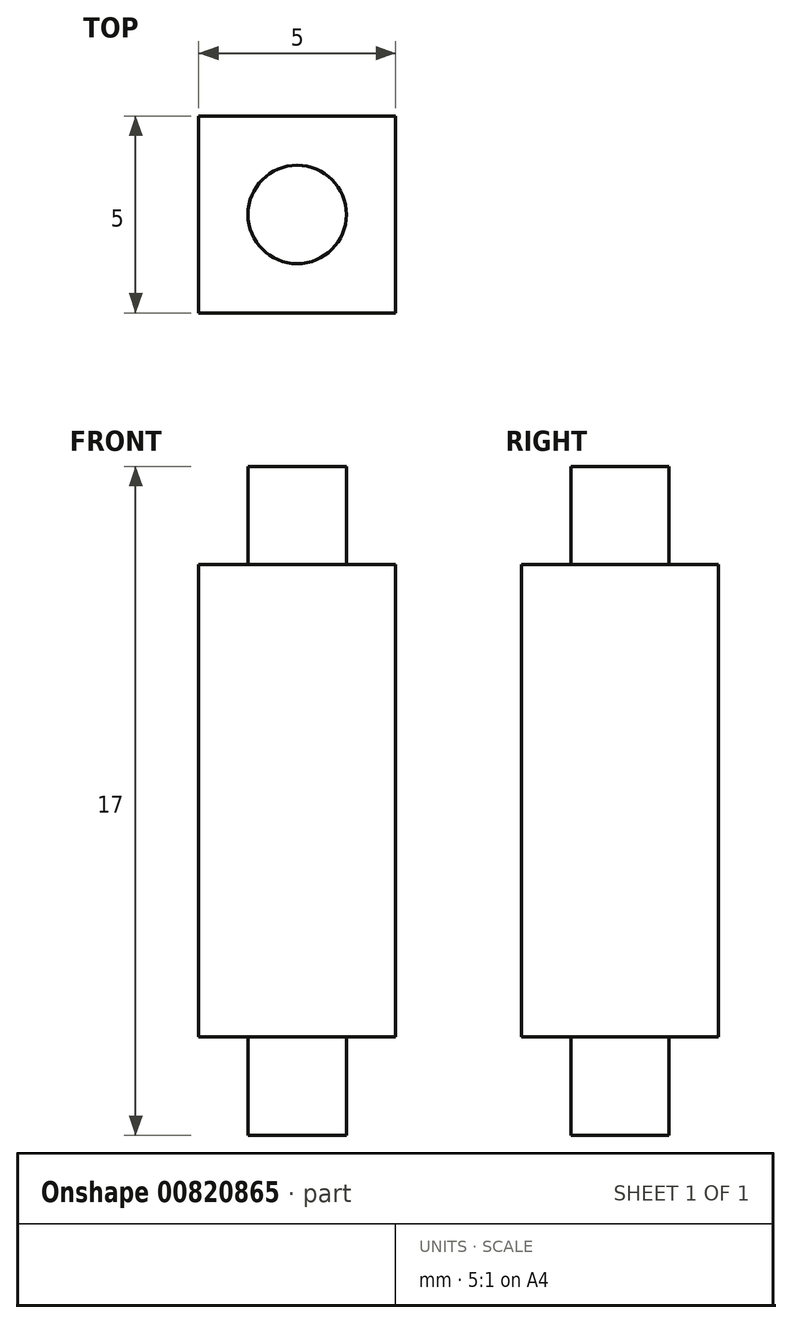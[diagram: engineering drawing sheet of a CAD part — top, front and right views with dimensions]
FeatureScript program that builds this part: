
annotation { "Feature Type Name" : "Feature", "Feature Type Description" : "" }
export const myFeature = defineFeature(function(context is Context, id is Id, definition is map)
    precondition{}
    {
        {
            var Q0;
            Q0=qCreatedBy(makeId("Top.planeOp"),FACE);
            var sketch = newSketch(context, id + "F0", { "sketchPlane" : qUnion([Q0])});
            skLineSegment(sketch, "E0.bottom", {"start": v(2.5, -2.5) * mm, "end": v(-2.5, -2.5) * mm});
            skLineSegment(sketch, "E0.top", {"start": v(2.5, 2.5) * mm, "end": v(-2.5, 2.5) * mm});
            skLineSegment(sketch, "E0.left", {"start": v(2.5, -2.5) * mm, "end": v(2.5, 2.5) * mm});
            skLineSegment(sketch, "E0.right", {"start": v(-2.5, -2.5) * mm, "end": v(-2.5, 2.5) * mm});
            skPoint(sketch, "E0.middle", {"position": v(0, 0) * mm});
            skSolve(sketch);
        }
        {
            var Q0;
            Q0 = qSketchRegion(id + "F0", true);
            extrude(context, id + "F1", {"entities" : qUnion([Q0]), "endBound" : BoundingType.SYMMETRIC, "depth" : 12 * mm, "offsetDistance" : 25 * mm});
        }
        {
            var Q0;
            Q0=makeQuery(id+"F1.opExtrude","CAP_FACE",FACE,{"disambiguationData":[OSD([sQuery(id+"F0.wireOp",EDGE,"E0.bottom"),sQuery(id+"F0.wireOp",EDGE,"E0.top"),sQuery(id+"F0.wireOp",EDGE,"E0.left"),sQuery(id+"F0.wireOp",EDGE,"E0.right")])],"isStart":false});
            var sketch = newSketch(context, id + "F2", { "sketchPlane" : qUnion([Q0])});
            skCircle(sketch, "E1", {"center": v(0, 0) * mm, "radius": 1.25 * mm});
            skSolve(sketch);
        }
        {
            var Q0;
            Q0 = qSketchRegion(id + "F2", true);
            extrude(context, id + "F3", {"entities" : qUnion([Q0]), "operationType" : NewBodyOperationType.ADD, "depth" : 2.5 * mm, "offsetDistance" : 25 * mm});
        }
        {
            var Q0;
            Q0=makeQuery(id+"F1.opExtrude","SWEPT_BODY",BODY,{"disambiguationData":[OSD([sQuery(id+"F0.wireOp",EDGE,"E0.bottom"),sQuery(id+"F0.wireOp",EDGE,"E0.top"),sQuery(id+"F0.wireOp",EDGE,"E0.left"),sQuery(id+"F0.wireOp",EDGE,"E0.right")])]});
            var Q1;
            Q1=qCreatedBy(makeId("Top.planeOp"),FACE);
            mirror(context, id + "F4", {"operationType" : NewBodyOperationType.ADD, "entities" : qUnion([Q0]), "mirrorPlane" : qUnion([Q1])});
        }
    });
